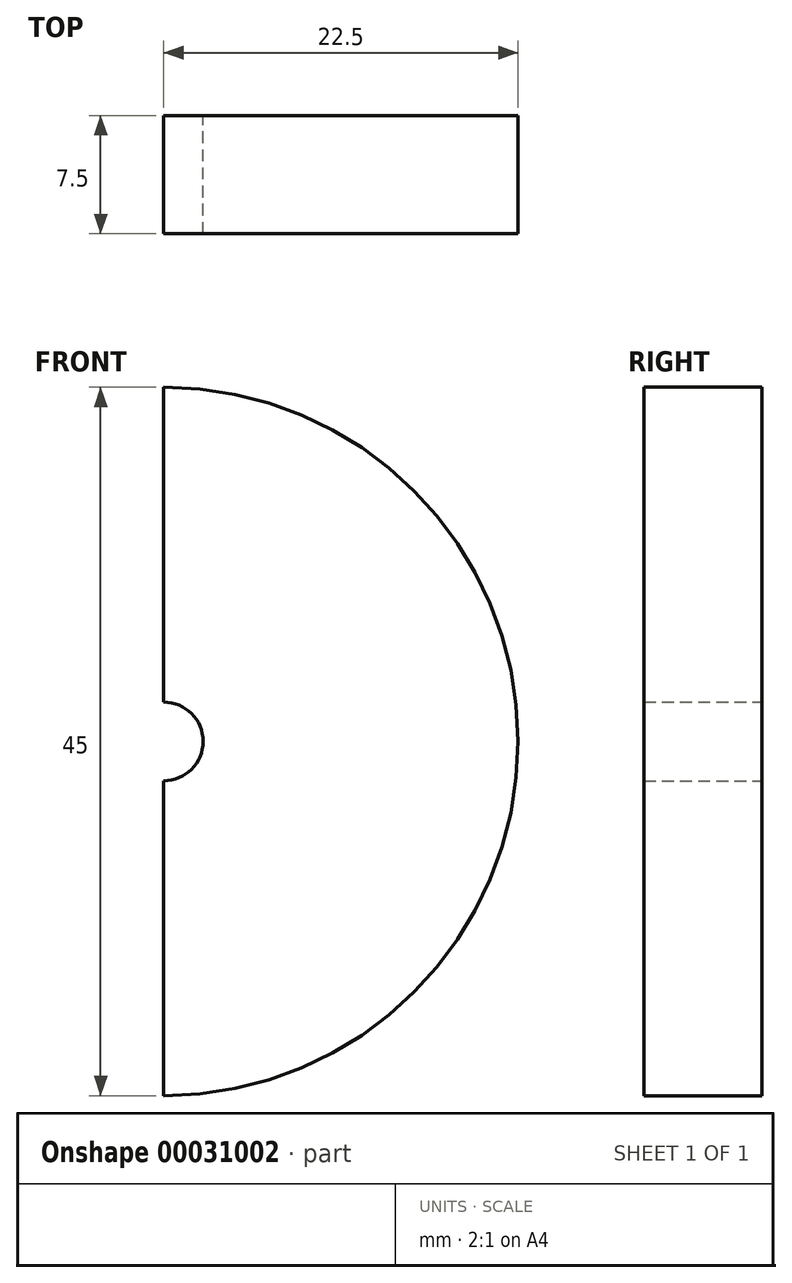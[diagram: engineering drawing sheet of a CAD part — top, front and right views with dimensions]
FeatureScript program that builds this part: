
annotation { "Feature Type Name" : "Feature", "Feature Type Description" : "" }
export const myFeature = defineFeature(function(context is Context, id is Id, definition is map)
    precondition{}
    {
        {
            var Q0;
            Q0=qCreatedBy(makeId("Front.planeOp"),FACE);
            var sketch = newSketch(context, id + "F0", { "sketchPlane" : qUnion([Q0])});
            skArc(sketch, "E0", {"start": v(0, -22.5) * mm, "mid": v(22.5, 0) * mm, "end": v(0, 22.5) * mm});
            skLineSegment(sketch, "E1", {"start": v(0, 22.5) * mm, "end": v(0, 2.5) * mm});
            skLineSegment(sketch, "E2", {"start": v(0, -22.5) * mm, "end": v(0, -2.5) * mm});
            skArc(sketch, "E3", {"start": v(0, -2.5) * mm, "mid": v(2.5, 0) * mm, "end": v(0, 2.5) * mm});
            skSolve(sketch);
        }
        {
            var Q0;
            Q0=makeQuery(id+"F0.imprint","IMPRINT",FACE,{"disambiguationData":[TD([[makeQuery(id+"F0.imprint","IMPRINT",EDGE,{"derivedFrom":sQuery(id+"F0.wireOp",EDGE,"E0")}),1.0]])]});
            extrude(context, id + "F1", {"entities" : qUnion([Q0]), "depth" : 7.5 * mm});
        }
    });
